# Revit family: Gira_011330
name_source: partatom
category: Electrical Fixtures
revit_build: Autodesk Revit 2017 (Build: 20160225_1515(x64)
units: mm (PartAtom-declared; Revit-internal decimal feet)

## family parameters
Cut with Voids When Loaded = No
Host = Face
Maintain Annotation Orientation = Yes
Part Type = Normal
Room Calculation Point = No
Round Connector Dimension = Use Diameter
Shared = No

## types (1)
- Rocker ind. sw. CB 3-p in.sp. WP surface-mounted grey
    Assembly arrangement = Basic element with complete housing
    Available = No
    BIM (1) = https://media.stage.bim.site und Tasten.rfa?public/gira/36a6b08/IP44_Komplettgerät_Schalten und Tasten.rfa
    Category = Switch
    Colour = Grey
    Connection type = Screwed terminal
    Data sheet (1) = https://katalog.gira.de
    Default Elevation = 1219 mm
    Description = Rock.ind.sw.CB 3-p in.sp. WP SM GY,Rocker indicator switch 16 A 400 V~ with inscription space,Circuit breaker 3-pole ,grey,Features:,- With screw terminals.,- With neon lamp element.,,Notes :,- Can also be connected with illumination.
    Function lighting = Illuminated (on)
    GTIN = 4010337113300
    HAN = 011330
    Halogen free = No
    HeinzeBIM = https://bimportal.heinze.de
    Illumination = Yes
    Label space/information surface = Yes
    Manufacturer = Gira
    Manufacturer URL = https://www.gira.de
    Material = Other
    Material quality = Other
    Method of operation = Rocker/button
    Mounting method = Surface mounted (plaster)
    Name = Rocker ind. sw. CB 3-p in.sp. WP surface-mounted grey
    Nominal voltage = 250
    Number of modules (module system) = 1
    Number of rockers = 1
    Push button switch = No
    Rated current = 10
    Suitable for degree of protection (IP) = IP44
    Surface protection = Other
    Type of fastening = Screw mounting
    Type of lighting = Glow lamp
    URL = http://katalog.gira.de
    Washing machine switch = No
    Wiring system = 3-pole switch

## geometry (parser evidence)
native form markers: Sweep x1
no freeform markers — native parametric forms only
